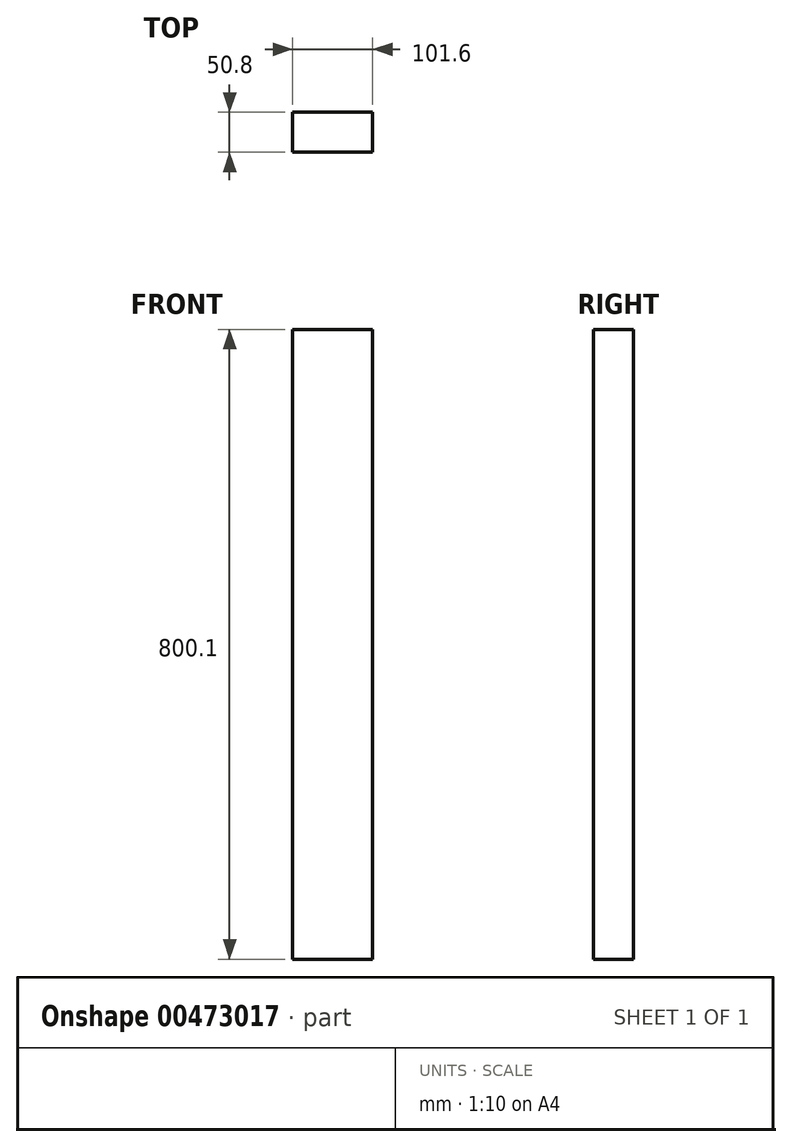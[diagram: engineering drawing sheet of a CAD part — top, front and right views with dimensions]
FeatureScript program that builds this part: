
annotation { "Feature Type Name" : "Feature", "Feature Type Description" : "" }
export const myFeature = defineFeature(function(context is Context, id is Id, definition is map)
    precondition{}
    {
        {
            var Q0;
            Q0=qCreatedBy(makeId("Top.planeOp"),FACE);
            var sketch = newSketch(context, id + "F0", { "sketchPlane" : qUnion([Q0])});
            skLineSegment(sketch, "E0.bottom", {"start": v(50.8, 25.4) * mm, "end": v(-50.8, 25.4) * mm});
            skLineSegment(sketch, "E0.top", {"start": v(50.8, -25.4) * mm, "end": v(-50.8, -25.4) * mm});
            skLineSegment(sketch, "E0.left", {"start": v(50.8, 25.4) * mm, "end": v(50.8, -25.4) * mm});
            skLineSegment(sketch, "E0.right", {"start": v(-50.8, 25.4) * mm, "end": v(-50.8, -25.4) * mm});
            skPoint(sketch, "E0.middle", {"position": v(0, 0) * mm});
            skSolve(sketch);
        }
        {
            var Q0;
            Q0 = qSketchRegion(id + "F0", true);
            extrude(context, id + "F1", {"entities" : qUnion([Q0]), "depth" : 800.1 * mm, "offsetDistance" : 25.4 * mm});
        }
    });
